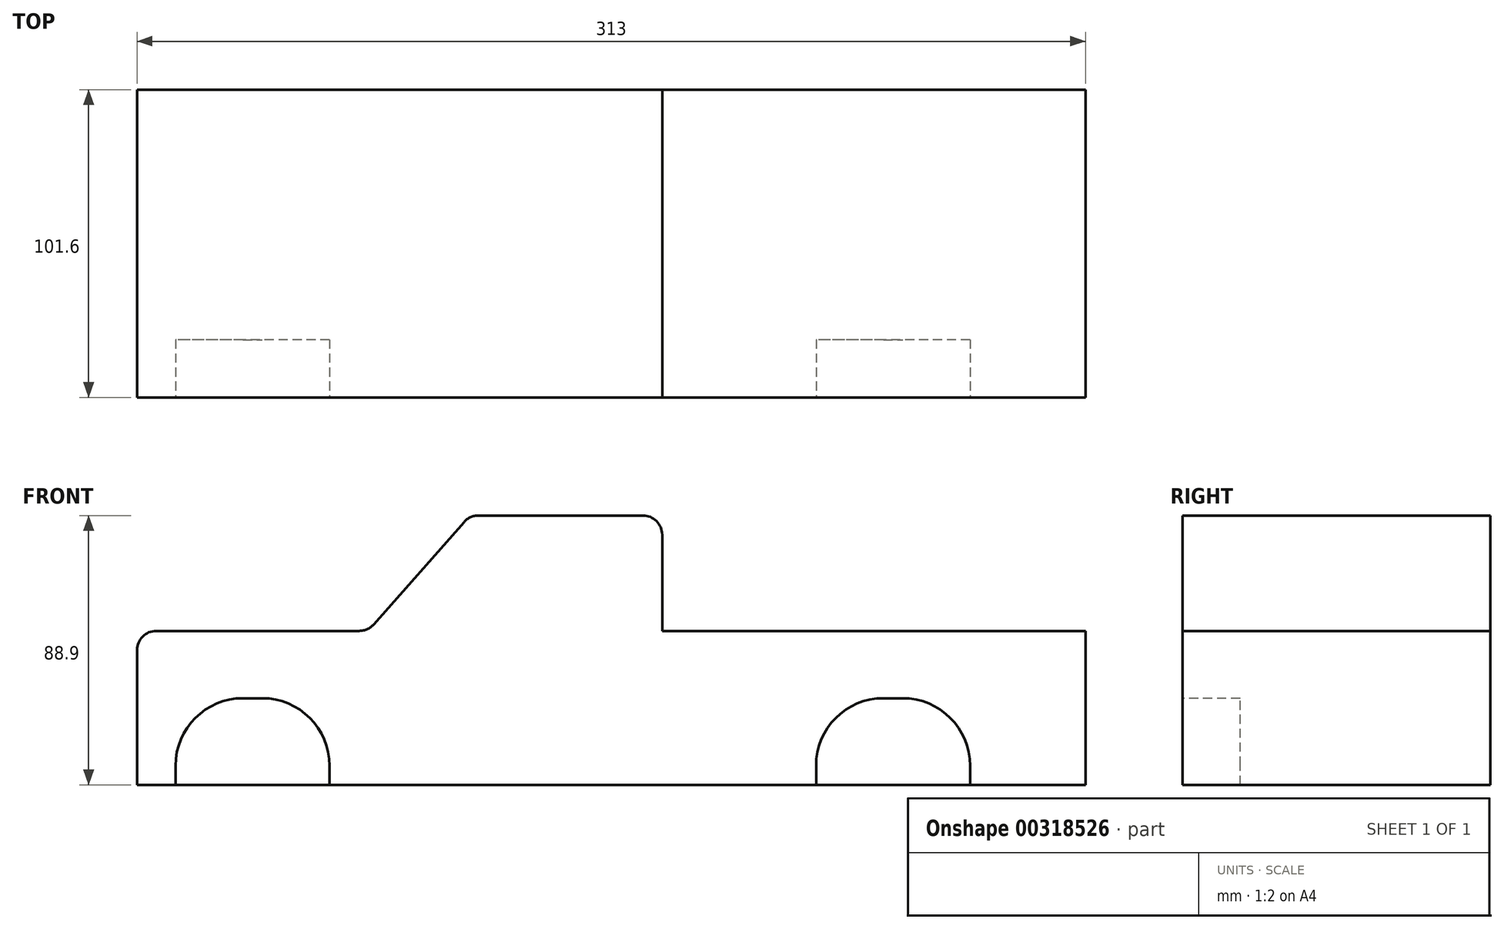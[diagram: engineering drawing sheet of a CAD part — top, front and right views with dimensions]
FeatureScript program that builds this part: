
annotation { "Feature Type Name" : "Feature", "Feature Type Description" : "" }
export const myFeature = defineFeature(function(context is Context, id is Id, definition is map)
    precondition{}
    {
        {
            var Q0;
            Q0=qCreatedBy(makeId("Front.planeOp"),FACE);
            var sketch = newSketch(context, id + "F0", { "sketchPlane" : qUnion([Q0])});
            skLineSegment(sketch, "E0", {"start": v(-138.38, 25.84) * mm, "end": v(-71.4, 25.84) * mm});
            skLineSegment(sketch, "E1", {"start": v(-66.64, 28) * mm, "end": v(-36.83, 61.8) * mm});
            skLineSegment(sketch, "E2", {"start": v(-32.07, 63.94) * mm, "end": v(22.22, 63.94) * mm});
            skLineSegment(sketch, "E3", {"start": v(28.57, 57.6) * mm, "end": v(28.57, 25.84) * mm});
            skLineSegment(sketch, "E4", {"start": v(28.57, 25.84) * mm, "end": v(168.27, 25.84) * mm});
            skLineSegment(sketch, "E5", {"start": v(168.27, 25.84) * mm, "end": v(168.27, -24.96) * mm});
            skLineSegment(sketch, "E6", {"start": v(168.27, -24.96) * mm, "end": v(134.67, -24.96) * mm});
            skLineSegment(sketch, "E7", {"start": v(134.67, -24.96) * mm, "end": v(134.67, -18.6) * mm});
            skLineSegment(sketch, "E8", {"start": v(112.44, 3.62) * mm, "end": v(106.1, 3.62) * mm});
            skLineSegment(sketch, "E9", {"start": v(83.87, -18.6) * mm, "end": v(83.87, -24.96) * mm});
            skLineSegment(sketch, "E10", {"start": v(83.87, -24.96) * mm, "end": v(-68.53, -24.96) * mm});
            skLineSegment(sketch, "E11", {"start": v(-68.53, -24.96) * mm, "end": v(-68.53, -18.6) * mm});
            skLineSegment(sketch, "E12", {"start": v(-90.76, 3.62) * mm, "end": v(-97.1, 3.62) * mm});
            skLineSegment(sketch, "E13", {"start": v(-119.33, -18.6) * mm, "end": v(-119.33, -24.96) * mm});
            skLineSegment(sketch, "E14", {"start": v(-119.33, -24.96) * mm, "end": v(-144.73, -24.96) * mm});
            skLineSegment(sketch, "E15", {"start": v(-144.73, -24.96) * mm, "end": v(-144.73, 19.5) * mm});
            skPoint(sketch, "E16.visualSharp", {"position": v(83.87, 3.62) * mm});
            skArc(sketch, "E16.filletArc", {"start": v(106.1, 3.62) * mm, "mid": v(90.38, -2.9) * mm, "end": v(83.87, -18.6) * mm});
            skPoint(sketch, "E17.visualSharp", {"position": v(134.67, 3.62) * mm});
            skArc(sketch, "E17.filletArc", {"start": v(134.67, -18.6) * mm, "mid": v(128.16, -2.9) * mm, "end": v(112.44, 3.62) * mm});
            skPoint(sketch, "E18.visualSharp", {"position": v(-119.33, 3.62) * mm});
            skArc(sketch, "E18.filletArc", {"start": v(-97.1, 3.62) * mm, "mid": v(-112.82, -2.9) * mm, "end": v(-119.33, -18.6) * mm});
            skPoint(sketch, "E19.visualSharp", {"position": v(-68.53, 3.62) * mm});
            skArc(sketch, "E19.filletArc", {"start": v(-68.53, -18.6) * mm, "mid": v(-75.04, -2.9) * mm, "end": v(-90.76, 3.62) * mm});
            skPoint(sketch, "E20.visualSharp", {"position": v(-144.73, 25.84) * mm});
            skArc(sketch, "E20.filletArc", {"start": v(-138.38, 25.84) * mm, "mid": v(-142.87, 23.98) * mm, "end": v(-144.73, 19.5) * mm});
            skPoint(sketch, "E21.visualSharp", {"position": v(28.57, 63.94) * mm});
            skArc(sketch, "E21.filletArc", {"start": v(28.57, 57.6) * mm, "mid": v(26.7, 62.08) * mm, "end": v(22.22, 63.94) * mm});
            skPoint(sketch, "E22.visualSharp", {"position": v(-34.93, 63.94) * mm});
            skArc(sketch, "E22.filletArc", {"start": v(-32.07, 63.94) * mm, "mid": v(-34.68, 63.38) * mm, "end": v(-36.83, 61.8) * mm});
            skPoint(sketch, "E23.visualSharp", {"position": v(-68.53, 25.84) * mm});
            skArc(sketch, "E23.filletArc", {"start": v(-71.4, 25.84) * mm, "mid": v(-68.79, 26.4) * mm, "end": v(-66.64, 28) * mm});
            skLineSegment(sketch, "E24", {"start": v(-119.33, -24.96) * mm, "end": v(-68.53, -24.96) * mm});
            skLineSegment(sketch, "E25", {"start": v(83.87, -24.96) * mm, "end": v(134.67, -24.96) * mm});
            skSolve(sketch);
        }
        {
            var Q0;
            Q0=makeQuery(id+"F0.imprint","IMPRINT",FACE,{"disambiguationData":[TD([[makeQuery(id+"F0.imprint","IMPRINT",EDGE,{"derivedFrom":sQuery(id+"F0.wireOp",EDGE,"E0")}),-1.0]])]});
            var Q1;
            Q1=makeQuery(id+"F0.imprint","IMPRINT",FACE,{"disambiguationData":[TD([[makeQuery(id+"F0.imprint","IMPRINT",EDGE,{"derivedFrom":sQuery(id+"F0.wireOp",EDGE,"E11")}),1.0]])]});
            var Q2;
            Q2=makeQuery(id+"F0.imprint","IMPRINT",FACE,{"disambiguationData":[TD([[makeQuery(id+"F0.imprint","IMPRINT",EDGE,{"derivedFrom":sQuery(id+"F0.wireOp",EDGE,"E7")}),1.0]])]});
            extrude(context, id + "F1", {"entities" : qUnion([Q0, Q1, Q2]), "endBound" : BoundingType.SYMMETRIC, "depth" : 101.6 * mm});
        }
        {
            var Q0;
            Q0=makeQuery(id+"F1.opExtrude","CAP_FACE",FACE,{"disambiguationData":[OSD([sQuery(id+"F0.wireOp",EDGE,"E0"),sQuery(id+"F0.wireOp",EDGE,"E1"),sQuery(id+"F0.wireOp",EDGE,"E2"),sQuery(id+"F0.wireOp",EDGE,"E3"),sQuery(id+"F0.wireOp",EDGE,"E4"),sQuery(id+"F0.wireOp",EDGE,"E5"),sQuery(id+"F0.wireOp",EDGE,"E6"),sQuery(id+"F0.wireOp",EDGE,"E10"),sQuery(id+"F0.wireOp",EDGE,"E14"),sQuery(id+"F0.wireOp",EDGE,"E15"),sQuery(id+"F0.wireOp",EDGE,"E20.filletArc"),sQuery(id+"F0.wireOp",EDGE,"E21.filletArc"),sQuery(id+"F0.wireOp",EDGE,"E22.filletArc"),sQuery(id+"F0.wireOp",EDGE,"E23.filletArc"),sQuery(id+"F0.wireOp",EDGE,"E24"),sQuery(id+"F0.wireOp",EDGE,"E25")])],"isStart":false});
            var sketch = newSketch(context, id + "F2", { "sketchPlane" : qUnion([Q0])});
            skLineSegment(sketch, "E26", {"start": v(-132.03, -24.96) * mm, "end": v(-132.03, -18.6) * mm});
            skLineSegment(sketch, "E27", {"start": v(-109.8, 3.62) * mm, "end": v(-103.46, 3.62) * mm});
            skLineSegment(sketch, "E28", {"start": v(-81.23, -18.6) * mm, "end": v(-81.23, -24.96) * mm});
            skLineSegment(sketch, "E29", {"start": v(79.37, -24.96) * mm, "end": v(79.37, -18.6) * mm});
            skLineSegment(sketch, "E30", {"start": v(101.6, 3.62) * mm, "end": v(107.94, 3.62) * mm});
            skLineSegment(sketch, "E31", {"start": v(130.17, -18.6) * mm, "end": v(130.17, -24.96) * mm});
            skPoint(sketch, "E32.visualSharp", {"position": v(-132.03, 3.62) * mm});
            skArc(sketch, "E32.filletArc", {"start": v(-109.8, 3.62) * mm, "mid": v(-125.52, -2.9) * mm, "end": v(-132.03, -18.6) * mm});
            skPoint(sketch, "E33.visualSharp", {"position": v(-81.23, 3.62) * mm});
            skArc(sketch, "E33.filletArc", {"start": v(-81.23, -18.6) * mm, "mid": v(-87.74, -2.9) * mm, "end": v(-103.46, 3.62) * mm});
            skPoint(sketch, "E34.visualSharp", {"position": v(79.37, 3.62) * mm});
            skArc(sketch, "E34.filletArc", {"start": v(101.6, 3.62) * mm, "mid": v(85.88, -2.9) * mm, "end": v(79.37, -18.6) * mm});
            skPoint(sketch, "E35.visualSharp", {"position": v(130.17, 3.62) * mm});
            skArc(sketch, "E35.filletArc", {"start": v(130.17, -18.6) * mm, "mid": v(123.66, -2.9) * mm, "end": v(107.94, 3.62) * mm});
            skSolve(sketch);
        }
        {
            var Q0;
            {var subQ1=sQuery(id+"F2.wireOp",EDGE,"E26");Q0=makeQuery(id+"F2.imprint","IMPRINT",FACE,{"disambiguationData":[TD([[makeQuery(id+"F2.imprint","IMPRINT",EDGE,{"derivedFrom":subQ1}),-1.0]])]});}
            var Q1;
            {var subQ1=sQuery(id+"F2.wireOp",EDGE,"E29");Q1=makeQuery(id+"F2.imprint","IMPRINT",FACE,{"disambiguationData":[TD([[makeQuery(id+"F2.imprint","IMPRINT",EDGE,{"derivedFrom":subQ1}),-1.0]])]});}
            extrude(context, id + "F3", {"entities" : qUnion([Q0, Q1]), "operationType" : NewBodyOperationType.REMOVE, "oppositeDirection" : true, "depth" : 19.05 * mm});
        }
    });
